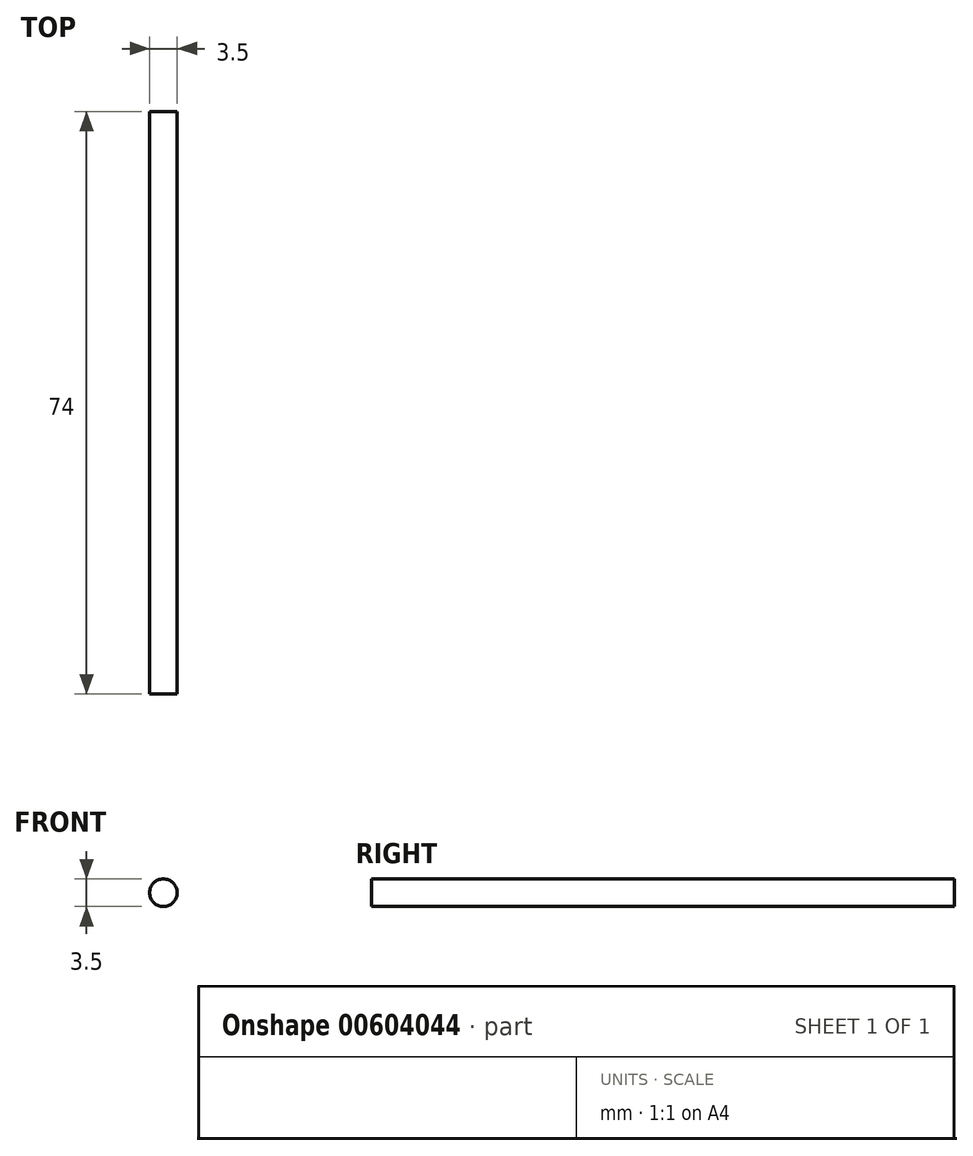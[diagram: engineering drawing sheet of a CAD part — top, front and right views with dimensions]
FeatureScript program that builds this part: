
annotation { "Feature Type Name" : "Feature", "Feature Type Description" : "" }
export const myFeature = defineFeature(function(context is Context, id is Id, definition is map)
    precondition{}
    {
        {
            var Q0;
            Q0=qCreatedBy(makeId("Front.planeOp"),FACE);
            var sketch = newSketch(context, id + "F0", { "sketchPlane" : qUnion([Q0])});
            skCircle(sketch, "E0", {"center": v(0, 0) * mm, "radius": 1.75 * mm});
            skSolve(sketch);
        }
        {
            var Q0;
            Q0=qSketchRegion(id+"F0",true);
            extrude(context, id + "F1", {"entities" : qUnion([Q0]), "depth" : 74 * mm});
        }
    });
